# Revit family: Sidewall-Propeller-Fan_LWBK_K-Series_Carnes
name_source: partatom
category: Mechanical Equipment
revit_build: Autodesk Revit Architecture 2012 (Build: 20110916_2132(x64)
units: mm (PartAtom-declared; Revit-internal decimal feet)

## types (6) — shared parameters
04 CSI = 23 34 16
95 CSI = 15830
Assembly Code = D3040200
D = 2.125 "
Description = Centrifugal Roof Exhausters
Housing = Aluminum-Carnes-Spun-Brushed
Manufacturer = Carnes Company
Manufacturer Fax = 608-845-6470
Product Page URL = http://www.carnes.com
URL = http://www.carnes.com
Warranty URL = http://www.carnes.com

## per-type parameters (varying)
| type | A | BE | Blade Radius | CE | E | F Dai Meter | F Radius | M Radius |
| LWBK 20 | 26 " | 23.625 " | 9.5 " | 18 " | 3.5 " | 20.5 " | 10.25 " | 2.375 " |
| LWBK 24 | 30 " | 23.625 " | 11.5 " | 18 " | 3.5 " | 24.5 " | 12.25 " | 2.875 " |
| LWBK 30 | 36 " | 26.625 " | 14.5 " | 21 " | 4.5 " | 30.5 " | 15.25 " | 3.625 " |
| LWBK 36 | 42 " | 28.625 " | 17.5 " | 23 " | 4.5 " | 36.5 " | 18.25 " | 4.375 " |
| LWBK 42 | 48 " | 28.625 " | 20.5 " | 23 " | 4.75 " | 42.5 " | 21.25 " | 5.125 " |
| LWBK 48 | 54 " | 28.625 " | 23.5 " | 23 " | 4.75 " | 48.5 " | 24.25 " | 5.875 " |

note: column(s) folded — value = type name in every type: Model

## geometry (parser evidence)
native form markers: Blend x4, Sweep x6
no freeform markers — native parametric forms only
